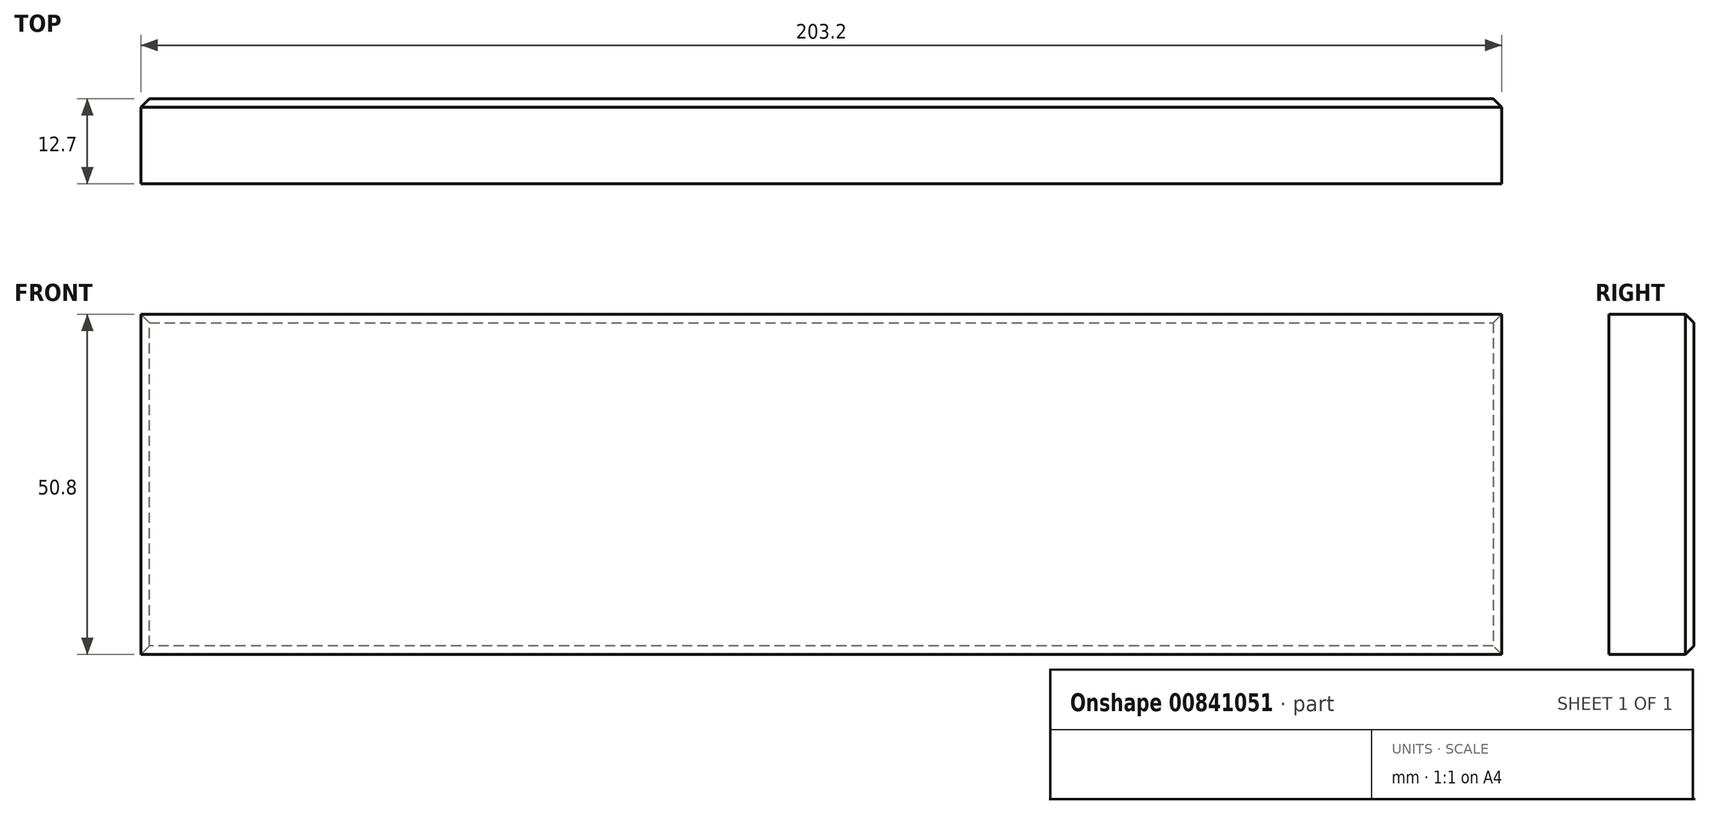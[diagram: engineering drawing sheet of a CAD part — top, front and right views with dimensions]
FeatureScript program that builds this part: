
annotation { "Feature Type Name" : "Feature", "Feature Type Description" : "" }
export const myFeature = defineFeature(function(context is Context, id is Id, definition is map)
    precondition{}
    {
        {
            var Q0;
            Q0=qCreatedBy(makeId("Front.planeOp"),FACE);
            var sketch = newSketch(context, id + "F0", { "sketchPlane" : qUnion([Q0])});
            skLineSegment(sketch, "E0.bottom", {"start": v(101.6, -25.4) * mm, "end": v(-101.6, -25.4) * mm});
            skLineSegment(sketch, "E0.top", {"start": v(101.6, 25.4) * mm, "end": v(-101.6, 25.4) * mm});
            skLineSegment(sketch, "E0.left", {"start": v(101.6, -25.4) * mm, "end": v(101.6, 25.4) * mm});
            skLineSegment(sketch, "E0.right", {"start": v(-101.6, -25.4) * mm, "end": v(-101.6, 25.4) * mm});
            skPoint(sketch, "E0.middle", {"position": v(0, 0) * mm});
            skSolve(sketch);
        }
        {
            var Q0;
            Q0 = qSketchRegion(id + "F0", true);
            extrude(context, id + "F1", {"entities" : qUnion([Q0]), "endBound" : BoundingType.SYMMETRIC, "depth" : 12.7 * mm, "offsetDistance" : 25.4 * mm});
        }
        {
            var Q0;
            Q0=qCreatedBy(makeId("Front.planeOp"),FACE);
            var sketch = newSketch(context, id + "F2", { "sketchPlane" : qUnion([Q0])});
            skCircle(sketch, "E1", {"center": v(-88.9, 12.7) * mm, "radius": 6.35 * mm});
            skCircle(sketch, "E2", {"center": v(-88.9, -12.7) * mm, "radius": 6.35 * mm});
            skCircle(sketch, "E3", {"center": v(88.9, 12.7) * mm, "radius": 6.35 * mm});
            skCircle(sketch, "E4", {"center": v(88.9, -12.7) * mm, "radius": 6.35 * mm});
            skSolve(sketch);
        }
        {
            var Q0;
            Q0=sQuery(id+"F2.wireOp",EDGE,"E1");
            var Q1;
            Q1=sQuery(id+"F2.wireOp",EDGE,"E2");
            var Q2;
            Q2=sQuery(id+"F2.wireOp",EDGE,"E3");
            var Q3;
            Q3=sQuery(id+"F2.wireOp",EDGE,"E4");
            extrude(context, id + "F3", {"bodyType" : ToolBodyType.SURFACE, "surfaceEntities" : qUnion([Q0, Q1, Q2, Q3]), "depth" : 76.2 * mm, "offsetDistance" : 25.4 * mm});
        }
        {
            var Q0;
            Q0=makeQuery(id+"F1.opExtrude","CAP_EDGE",EDGE,{"disambiguationData":[OSD([sQuery(id+"F0.wireOp",EDGE,"E0.right")])],"isStart":true});
            var Q1;
            Q1=makeQuery(id+"F1.opExtrude","CAP_EDGE",EDGE,{"disambiguationData":[OSD([sQuery(id+"F0.wireOp",EDGE,"E0.bottom")])],"isStart":true});
            var Q2;
            Q2=makeQuery(id+"F1.opExtrude","CAP_EDGE",EDGE,{"disambiguationData":[OSD([sQuery(id+"F0.wireOp",EDGE,"E0.top")])],"isStart":true});
            var Q3;
            Q3=makeQuery(id+"F1.opExtrude","CAP_EDGE",EDGE,{"disambiguationData":[OSD([sQuery(id+"F0.wireOp",EDGE,"E0.left")])],"isStart":true});
            chamfer(context, id + "F4", {"entities" : qUnion([Q0, Q1, Q2, Q3]), "width" : 1.27 * mm, "tangentPropagation" : true});
        }
    });
